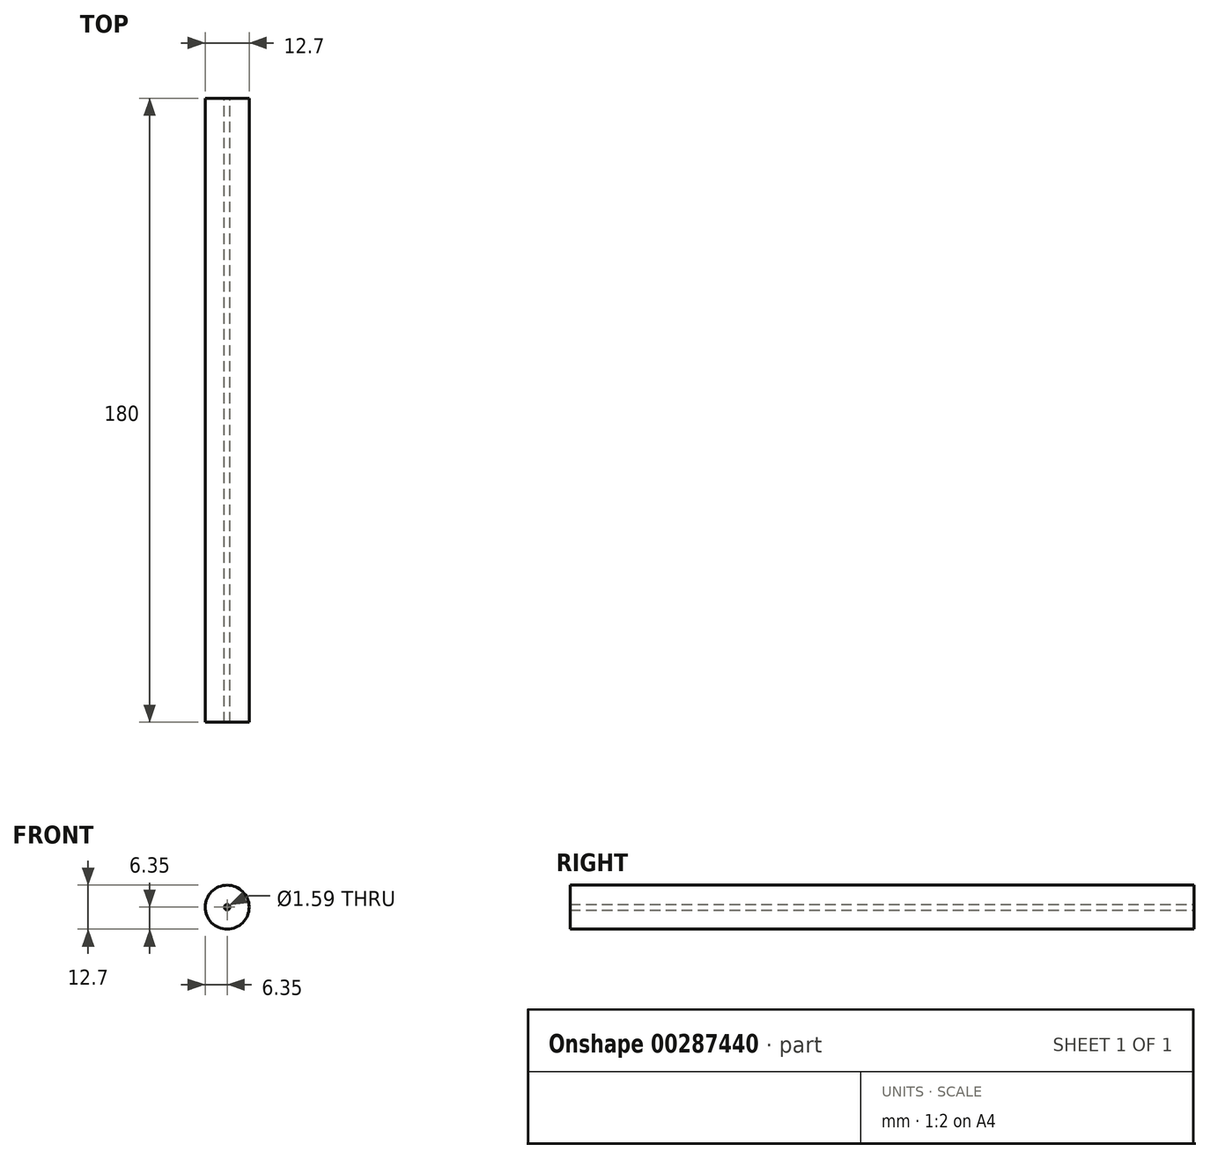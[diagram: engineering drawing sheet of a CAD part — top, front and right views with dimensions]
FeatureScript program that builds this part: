
annotation { "Feature Type Name" : "Feature", "Feature Type Description" : "" }
export const myFeature = defineFeature(function(context is Context, id is Id, definition is map)
    precondition{}
    {
        {
            var Q0;
            Q0=qCreatedBy(makeId("Front.planeOp"),FACE);
            var sketch = newSketch(context, id + "F0", { "sketchPlane" : qUnion([Q0])});
            skCircle(sketch, "E0", {"center": v(0, 0) * mm, "radius": 6.35 * mm});
            skCircle(sketch, "E1", {"center": v(0, 0) * mm, "radius": 0.8 * mm});
            skSolve(sketch);
        }
        {
            var Q0;
            Q0 = qSketchRegion(id + "F0", true);
            extrude(context, id + "F1", {"entities" : qUnion([Q0]), "depth" : 180 * mm});
        }
    });
